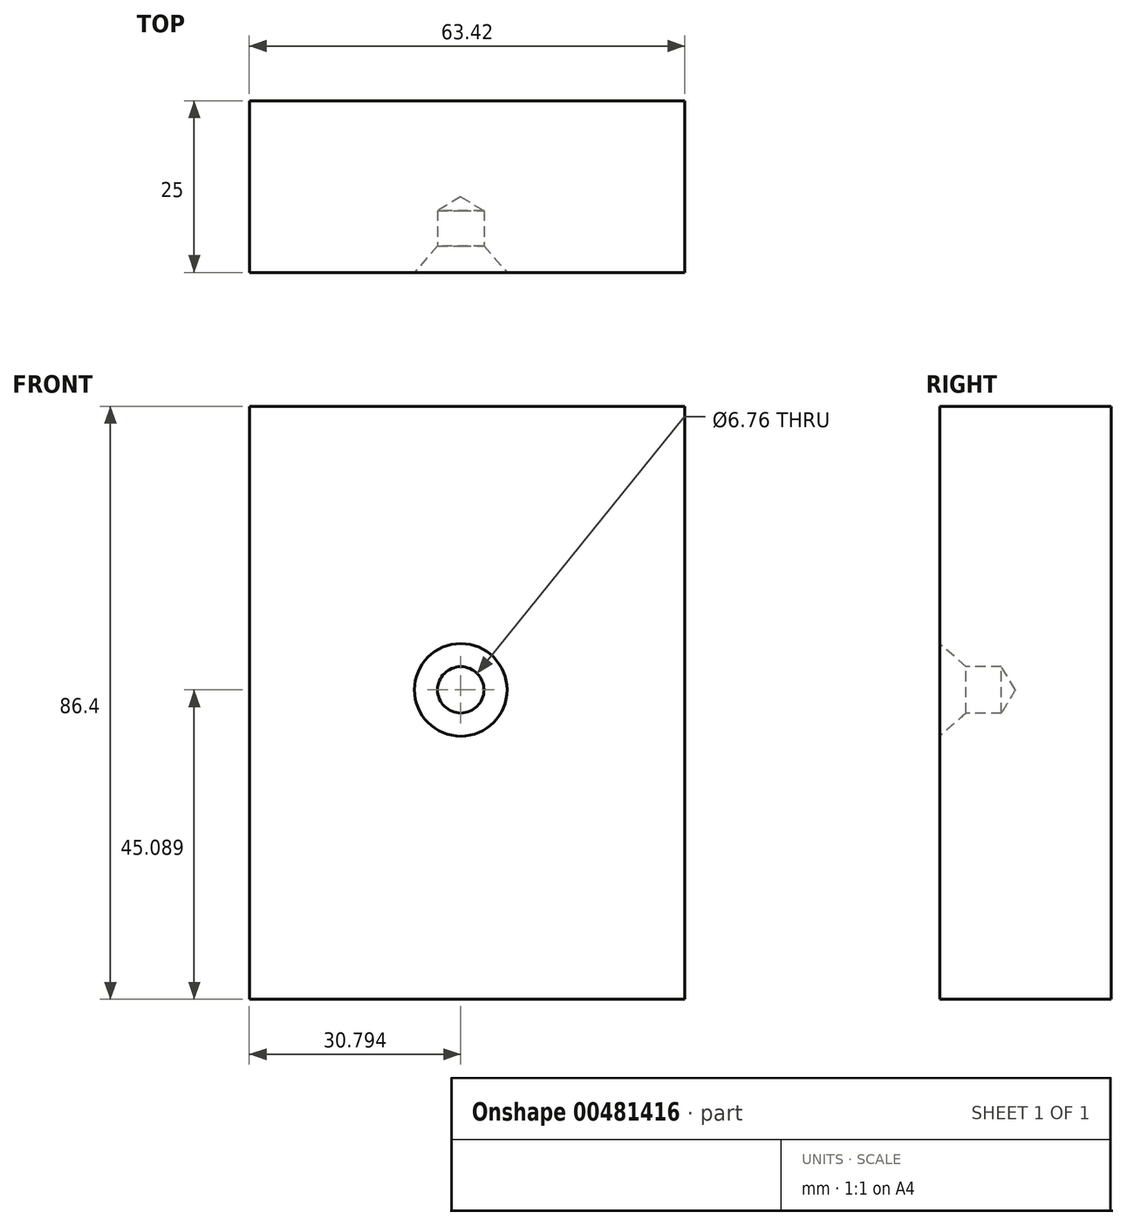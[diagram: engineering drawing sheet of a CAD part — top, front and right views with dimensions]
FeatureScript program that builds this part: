
annotation { "Feature Type Name" : "Feature", "Feature Type Description" : "" }
export const myFeature = defineFeature(function(context is Context, id is Id, definition is map)
    precondition{}
    {
        {
            var Q0;
            Q0=qCreatedBy(makeId("Front.planeOp"),FACE);
            var sketch = newSketch(context, id + "F0", { "sketchPlane" : qUnion([Q0])});
            skLineSegment(sketch, "E0.bottom", {"start": v(-116.83, -12.03) * mm, "end": v(-53.4, -12.03) * mm});
            skLineSegment(sketch, "E0.top", {"start": v(-116.83, 74.37) * mm, "end": v(-53.4, 74.37) * mm});
            skLineSegment(sketch, "E0.left", {"start": v(-116.83, -12.03) * mm, "end": v(-116.83, 74.37) * mm});
            skLineSegment(sketch, "E0.right", {"start": v(-53.4, -12.03) * mm, "end": v(-53.4, 74.37) * mm});
            skPoint(sketch, "E0.middle", {"position": v(-85.12, 31.17) * mm});
            skSolve(sketch);
        }
        {
            var Q0;
            Q0=makeQuery(id+"F0.imprint","IMPRINT",FACE,{"disambiguationData":[TD([[makeQuery(id+"F0.imprint","IMPRINT",EDGE,{"derivedFrom":sQuery(id+"F0.wireOp",EDGE,"E0.bottom")}),1.0]])]});
            extrude(context, id + "F1", {"entities" : qUnion([Q0]), "depth" : 25 * mm});
        }
        {
            var Q0;
            Q0=makeQuery(id+"F1.opExtrude","CAP_FACE",FACE,{"disambiguationData":[OSD([sQuery(id+"F0.wireOp",EDGE,"E0.bottom"),sQuery(id+"F0.wireOp",EDGE,"E0.top"),sQuery(id+"F0.wireOp",EDGE,"E0.left"),sQuery(id+"F0.wireOp",EDGE,"E0.right")])],"isStart":false});
            var sketch = newSketch(context, id + "F2", { "sketchPlane" : qUnion([Q0])});
            skPoint(sketch, "E1", {"position": v(-86.04, 33.06) * mm});
            skSolve(sketch);
        }
        {
            var Q0;
            Q0=sQuery(id+"F2.wireOp",VERTEX,"E1");
            var Q1;
            Q1=makeQuery(id+"F1.opExtrude","SWEPT_BODY",BODY,{"disambiguationData":[OSD([sQuery(id+"F0.wireOp",EDGE,"E0.bottom"),sQuery(id+"F0.wireOp",EDGE,"E0.top"),sQuery(id+"F0.wireOp",EDGE,"E0.left"),sQuery(id+"F0.wireOp",EDGE,"E0.right")])]});
            hole(context, id + "F3", {"style" : HoleStyle.C_SINK, "endStyle" : HoleEndStyle.BLIND, "standardTappedOrClearance" : lookupTablePath({ "standard" : "ANSI", "fit" : "Normal (ASME)", "size" : "1/4", "type" : "Clearance" }), "standardBlindInLast" : lookupTablePath({ "fit" : "Free", "standard" : "ANSI", "size" : "1/4", "type" : "Clearance" }), "holeDiameter" : 6.76 * mm, "cSinkDiameter" : 13.5 * mm, "cSinkAngle" : 82 * degree, "holeDepth" : 9 * mm, "isTappedThrough" : true, "tappedDepth" : 12 * mm, "tapClearance" : 3, "locations" : qUnion([Q0]), "scope" : qUnion([Q1])});
        }
        {
            var Q0;
            Q0=qCreatedBy(makeId("Front.planeOp"),FACE);
            var sketch = newSketch(context, id + "F4", { "sketchPlane" : qUnion([Q0])});
            skLineSegment(sketch, "E2", {"start": v(-32.71, 64) * mm, "end": v(-32.71, -25.61) * mm});
            skSolve(sketch);
        }
        {
            var Q0;
            Q0=sQuery(id+"F4.wireOp",EDGE,"E2");
            extrude(context, id + "F5", {"bodyType" : ToolBodyType.SURFACE, "surfaceEntities" : qUnion([Q0]), "depth" : 25 * mm});
        }
    });
